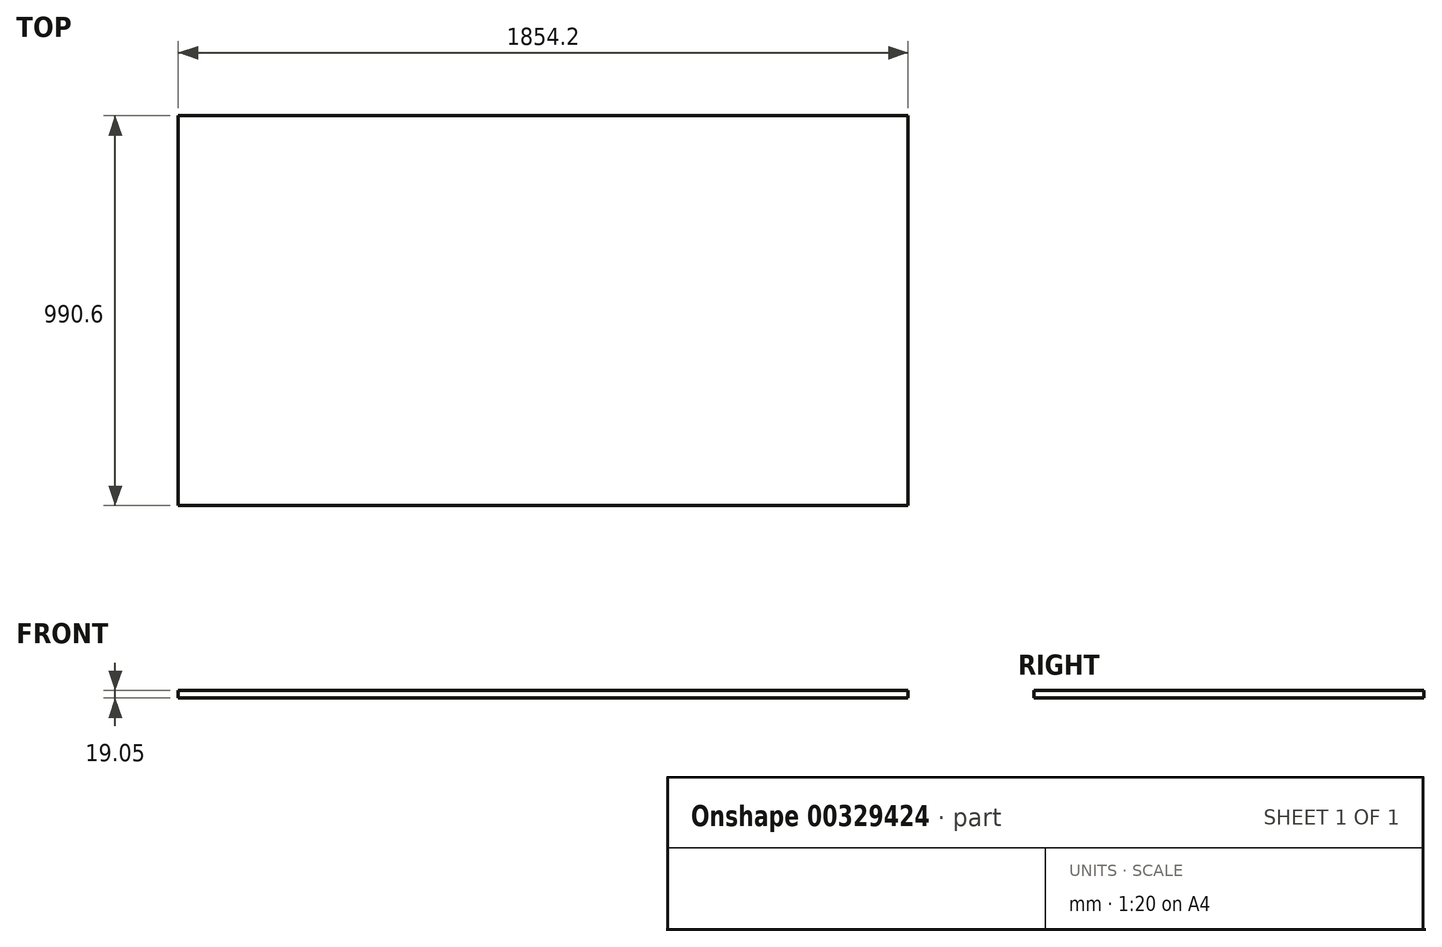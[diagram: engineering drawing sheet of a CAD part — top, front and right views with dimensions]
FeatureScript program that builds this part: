
annotation { "Feature Type Name" : "Feature", "Feature Type Description" : "" }
export const myFeature = defineFeature(function(context is Context, id is Id, definition is map)
    precondition{}
    {
        {
            var Q0;
            Q0=qCreatedBy(makeId("Top.planeOp"),FACE);
            var sketch = newSketch(context, id + "F0", { "sketchPlane" : qUnion([Q0])});
            skLineSegment(sketch, "E0.bottom", {"start": v(927.1, -495.3) * mm, "end": v(-927.1, -495.3) * mm});
            skLineSegment(sketch, "E0.top", {"start": v(927.1, 495.3) * mm, "end": v(-927.1, 495.3) * mm});
            skLineSegment(sketch, "E0.left", {"start": v(927.1, -495.3) * mm, "end": v(927.1, 495.3) * mm});
            skLineSegment(sketch, "E0.right", {"start": v(-927.1, -495.3) * mm, "end": v(-927.1, 495.3) * mm});
            skPoint(sketch, "E0.middle", {"position": v(0, 0) * mm});
            skSolve(sketch);
        }
        {
            var Q0;
            Q0 = qSketchRegion(id + "F0", true);
            extrude(context, id + "F1", {"entities" : qUnion([Q0]), "depth" : 19.05 * mm});
        }
    });
